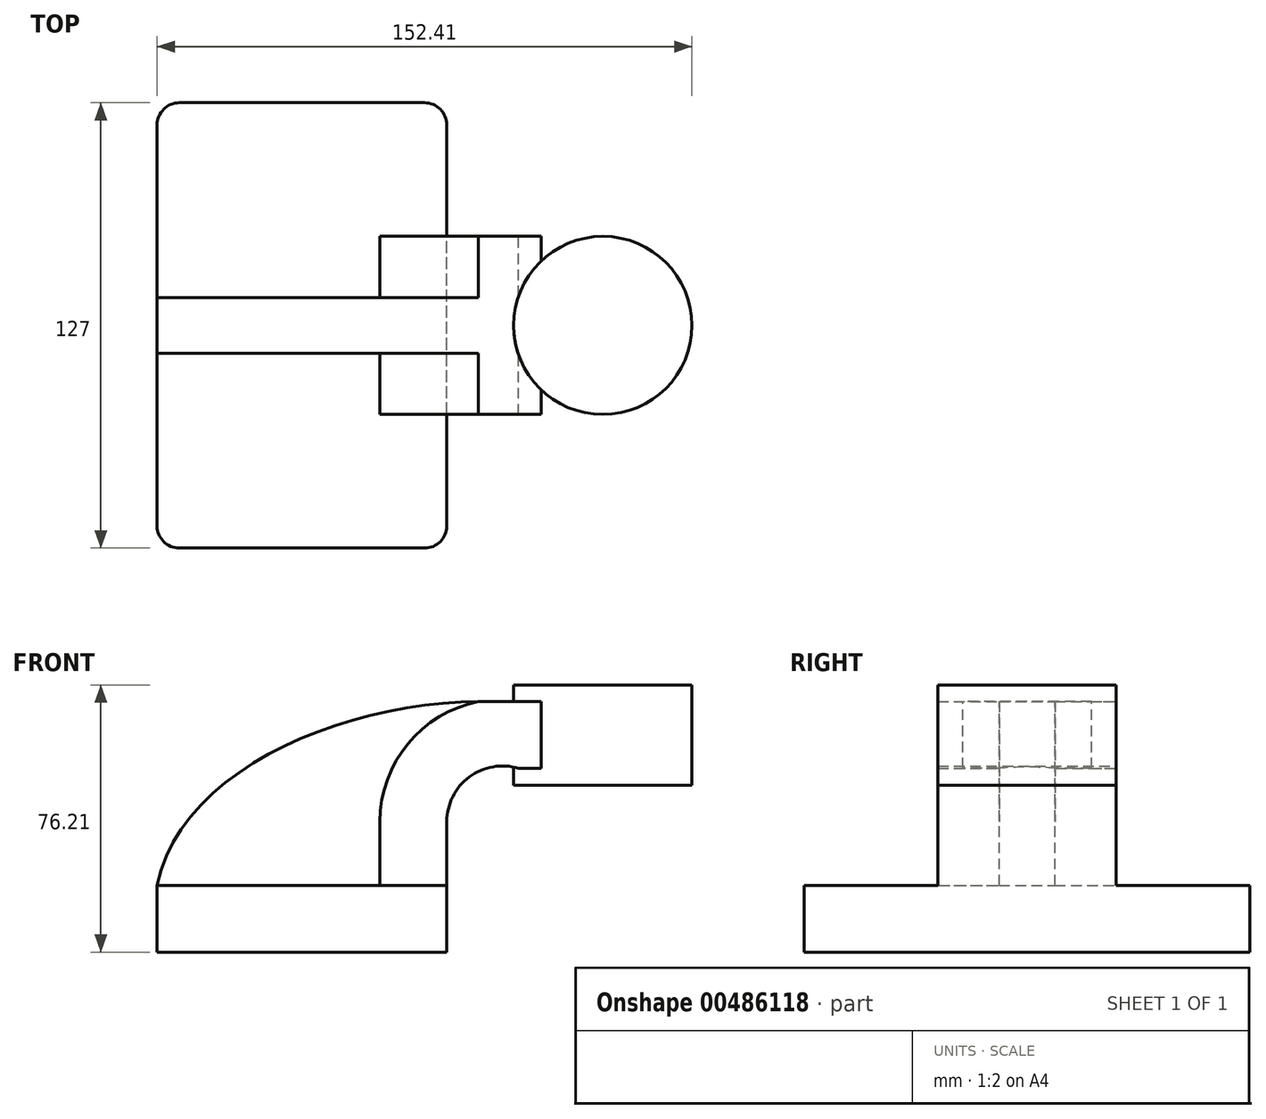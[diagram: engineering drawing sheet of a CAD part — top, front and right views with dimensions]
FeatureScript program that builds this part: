
annotation { "Feature Type Name" : "Feature", "Feature Type Description" : "" }
export const myFeature = defineFeature(function(context is Context, id is Id, definition is map)
    precondition{}
    {
        {
            var Q0;
            Q0=qCreatedBy(makeId("Front.planeOp"),FACE);
            var sketch = newSketch(context, id + "F0", { "sketchPlane" : qUnion([Q0])});
            skLineSegment(sketch, "E0.bottom", {"start": v(41.28, 9.53) * mm, "end": v(-41.28, 9.53) * mm});
            skLineSegment(sketch, "E0.top", {"start": v(41.28, -9.52) * mm, "end": v(-41.28, -9.52) * mm});
            skLineSegment(sketch, "E0.left", {"start": v(41.28, 9.53) * mm, "end": v(41.28, -9.52) * mm});
            skLineSegment(sketch, "E0.right", {"start": v(-41.28, 9.53) * mm, "end": v(-41.28, -9.52) * mm});
            skPoint(sketch, "E0.middle", {"position": v(0, 0) * mm});
            skLineSegment(sketch, "E1.bottom", {"start": v(111.12, 38.1) * mm, "end": v(60.32, 38.1) * mm});
            skLineSegment(sketch, "E1.top", {"start": v(111.13, 66.68) * mm, "end": v(60.33, 66.68) * mm});
            skLineSegment(sketch, "E1.left", {"start": v(111.12, 38.1) * mm, "end": v(111.12, 66.68) * mm});
            skLineSegment(sketch, "E1.right", {"start": v(60.32, 38.1) * mm, "end": v(60.32, 66.68) * mm});
            skPoint(sketch, "E1.middle", {"position": v(85.72, 52.39) * mm});
            skLineSegment(sketch, "E2", {"start": v(41.28, 9.53) * mm, "end": v(41.28, 27.67) * mm});
            skArc(sketch, "E3", {"start": v(41.28, 27.67) * mm, "mid": v(47.68, 40.41) * mm, "end": v(61.72, 42.88) * mm});
            skLineSegment(sketch, "E4", {"start": v(61.72, 42.88) * mm, "end": v(68.15, 42.88) * mm});
            skLineSegment(sketch, "E5.0", {"start": v(50.32, 61.93) * mm, "end": v(68.15, 61.93) * mm});
            skArc(sketch, "E5.1", {"start": v(22.23, 27.67) * mm, "mid": v(30.15, 49.83) * mm, "end": v(50.32, 61.93) * mm});
            skLineSegment(sketch, "E5.2", {"start": v(22.22, 9.53) * mm, "end": v(22.22, 27.67) * mm});
            skLineSegment(sketch, "E6", {"start": v(68.15, 42.88) * mm, "end": v(68.15, 61.93) * mm});
            skLineSegment(sketch, "E7", {"start": v(22.22, 9.53) * mm, "end": v(41.28, 9.53) * mm});
            skFitSpline(sketch, "E8", {"points": [v(-41.28, 9.52) * mm, v(50.32, 61.93) * mm], "startDerivative": vector(19.5, 99.35) * mm, "endDerivative": vector(114.21, 0.64) * mm});
            skLineSegment(sketch, "E9", {"start": v(85.72, 66.68) * mm, "end": v(85.72, 38.1) * mm});
            skSolve(sketch);
        }
        {
            var Q0;
            Q0=makeQuery(id+"F0.imprint","IMPRINT",FACE,{"disambiguationData":[TD([[makeQuery(id+"F0.imprint","IMPRINT",EDGE,{"derivedFrom":sQuery(id+"F0.wireOp",EDGE,"E0.bottom")}),1.0]])]});
            extrude(context, id + "F1", {"entities" : qUnion([Q0]), "endBound" : BoundingType.SYMMETRIC, "depth" : 127 * mm});
        }
        {
            var Q0;
            Q0=makeQuery(id+"F0.imprint","IMPRINT",FACE,{"disambiguationData":[TD([[makeQuery(id+"F0.imprint","IMPRINT",EDGE,{"derivedFrom":sQuery(id+"F0.wireOp",EDGE,"E0.bottom")}),-1.0]])]});
            extrude(context, id + "F2", {"entities" : qUnion([Q0]), "operationType" : NewBodyOperationType.ADD, "endBound" : BoundingType.SYMMETRIC, "depth" : 15.88 * mm});
        }
        {
            var Q0;
            {var subQ5=sQuery(id+"F0.wireOp",EDGE,"E2");Q0=makeQuery(id+"F0.imprint","IMPRINT",FACE,{"disambiguationData":[TD([[makeQuery(id+"F0.imprint","IMPRINT",EDGE,{"derivedFrom":subQ5}),1.0]])]});}
            var Q1;
            {var subQ4=sQuery(id+"F0.wireOp",EDGE,"E4");Q1=makeQuery(id+"F0.imprint","IMPRINT",FACE,{"disambiguationData":[TD([[makeQuery(id+"F0.imprint","IMPRINT",EDGE,{"derivedFrom":subQ4}),1.0]])]});}
            extrude(context, id + "F3", {"entities" : qUnion([Q0, Q1]), "operationType" : NewBodyOperationType.ADD, "endBound" : BoundingType.SYMMETRIC, "depth" : 50.8 * mm});
        }
        {
            var Q0;
            {var subQ0=sQuery(id+"F0.wireOp",EDGE,"E1.left");Q0=makeQuery(id+"F0.imprint","IMPRINT",FACE,{"disambiguationData":[TD([[makeQuery(id+"F0.imprint","IMPRINT",EDGE,{"derivedFrom":subQ0}),1.0]])]});}
            var Q1;
            Q1=sQuery(id+"F0.wireOp",EDGE,"E9");
            revolve(context, id + "F4", {"operationType" : NewBodyOperationType.ADD, "entities" : qUnion([Q0]), "axis" : qUnion([Q1]), "revolveType" : RevolveType.FULL});
        }
        {
            var Q0;
            Q0=makeQuery(id+"F1.opExtrude","CAP_EDGE",EDGE,{"disambiguationData":[OSD([sQuery(id+"F0.wireOp",EDGE,"E0.left")])],"isStart":false});
            var Q1;
            Q1=makeQuery(id+"F1.opExtrude","CAP_EDGE",EDGE,{"disambiguationData":[OSD([sQuery(id+"F0.wireOp",EDGE,"E0.right")])],"isStart":false});
            var Q2;
            Q2=makeQuery(id+"F1.opExtrude","CAP_EDGE",EDGE,{"disambiguationData":[OSD([sQuery(id+"F0.wireOp",EDGE,"E0.left")])],"isStart":true});
            var Q3;
            Q3=makeQuery(id+"F1.opExtrude","CAP_EDGE",EDGE,{"disambiguationData":[OSD([sQuery(id+"F0.wireOp",EDGE,"E0.right")])],"isStart":true});
            fillet(context, id + "F5", {"entities" : qUnion([Q0, Q1, Q2, Q3]), "radius" : 6.35 * mm, "tangentPropagation" : true, "allowEdgeOverflow" : false});
        }
    });
